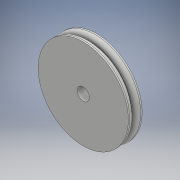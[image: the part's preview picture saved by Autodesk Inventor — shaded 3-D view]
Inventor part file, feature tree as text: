
AUTODESK INVENTOR PART (.ipt)
format: ipt  version: 2018 (Build 220112000, 112)  size: 302,080 bytes
history: native  units: mm
features: extrude x3, sketch x3, fillet x1
ambient origin geometry x8: Origin, YZ Plane, XZ Plane, XY Plane, X Axis, Y Axis, Z Axis, Center Point
bodies: Solid1 (feature_tree)
feature tree (7):
  extrude  "Extrusion1"  Depth=4.1mm
  extrude  "Extrusion2"  Depth=2.0mm
  extrude  "Extrusion3"  Depth=2.0mm TaperAngle=0.0deg
  fillet  "Fillet1"  Radius=1.5mm
  sketch  "Sketch1"  dims[d0=30.0mm d1=4.1mm]
  sketch  "Sketch2"  dims[d2=2.0mm d3=0.0mm d4=27.0mm]
  sketch  "Sketch3"  dims[d5=0.5mm d6=0.0mm d7=2.0mm d8=0.0mm d9=1.5mm]
